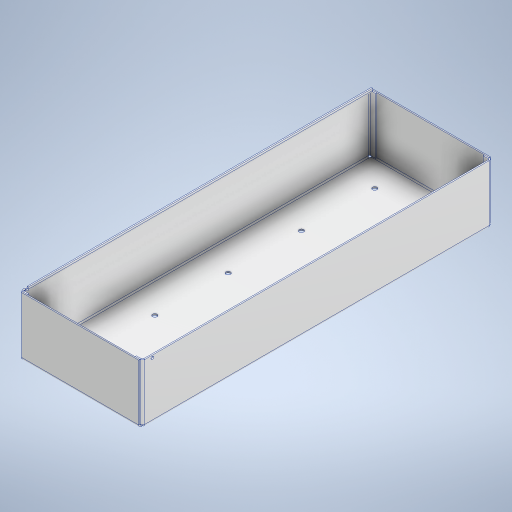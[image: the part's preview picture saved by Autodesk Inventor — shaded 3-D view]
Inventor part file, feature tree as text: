
AUTODESK INVENTOR PART (.ipt)
format: ipt  version: 2023 (Build 270158000, 158)  size: 440,320 bytes
history: native  units: in
note: dims shown in document units (in); Inventor stores cm internally (conversion verified against a paired STEP export)
features: sheet_metal_op x16, sketch x10, other x8, hole x2, pattern_linear x1
ambient origin geometry x8: Origin, YZ Plane, XZ Plane, XY Plane, X Axis, Y Axis, Z Axis, Center Point
bodies: Solid1 (feature_tree)
feature tree (37):
  sheet_metal_op  "Face1"
  hole  "Hole1"  [1 undecoded]
  pattern_linear  "Rectangular Pattern1"  Count1=30  [1 undecoded]
  sheet_metal_op  "Flange4"
  sheet_metal_op  "Flange5"
  sheet_metal_op  "Flange11"
  sheet_metal_op  "Flange12"
  sheet_metal_op  "Flange13"
  hole  "Hole2"  [1 undecoded]
  sketch  "Sketch1"  dims[d0=23.622in d1=7.874in d2=11.811in]
  other  "Plate1"
  sketch  "Sketch2"  dims[d3=3.937in d4=0.0875in]
  sketch  "Sketch6"  dims[d5=0.2969in d6=0.2953in d7=0.1476in d8=0.0984in d9=90.0deg d10=0.0875in]
  other  "Plate5"
  sheet_metal_op  "Bend4"
  sheet_metal_op  "Corner4"
  sketch  "Sketch7"  dims[d11=0.0in]
  other  "Plate6"
  sheet_metal_op  "Bend5"
  sheet_metal_op  "Corner5"
  sketch  "Sketch8"  dims[d12=1.9685in]
  sketch  "Sketch9"  dims[d13=2.0669in]
  sketch  "Sketch17"  dims[d14=0.7874in d16=3.937in]
  other  "Plate12"
  sheet_metal_op  "Bend11"
  sheet_metal_op  "Corner11"
  sketch  "Sketch18"  dims[d17=1.9685in d19=4.9213in]
  other  "Plate13"
  sheet_metal_op  "Bend12"
  sheet_metal_op  "Corner12"
  sketch  "Sketch19"  dims[d50=0.0875in]
  other  "Plate14"
  sheet_metal_op  "Bend13"
  sheet_metal_op  "Corner13"
  sketch  "Sketch20"  dims[d51=0.0438in d52=0.175in d53=0.0875in d54=3.937in d55=90.0deg d56=0.0787in d57=0.35in d58=0.0875in d59=0.0875in d60=0.0875in d61=0.0438in d62=0.175in d63=0.0875in d64=3.937in d65=90.0deg d66=0.0787in d67=0.35in d68=0.0875in d69=0.0875in d70=0.0098in d71=0.0591in d72=0.0098in d73=0.0591in d78=0.0875in d79=0.0in d80=0.0875in d81=0.0in d147=0.0875in d148=0.0438in d149=0.175in d150=0.0875in d151=0.4921in d152=90.0deg d153=0.0787in d154=0.35in d155=0.0875in d156=0.0875in d157=0.0875in d158=0.0438in d159=0.175in d160=0.0875in d161=0.2953in d162=90.0deg d163=0.0787in d164=0.35in d165=0.0875in d166=0.0875in d167=0.0875in d168=0.0438in d169=0.175in d170=0.0875in d171=0.2953in d172=90.0deg d173=0.0787in d174=0.35in d175=0.0875in d176=0.0875in d177=0.194in d178=0.2953in d179=0.1476in d180=0.0984in d181=90.0deg d182=0.0875in d183=0.8108in d184=0.162in d185=0.4994in]
  other  "Cut2"
  other  "Cut3"
note: 3 required parameter values undecoded (feature->parameter linkage not recoverable at this tier; creation-order binding heuristic only, values carry confidence <= 0.55)
